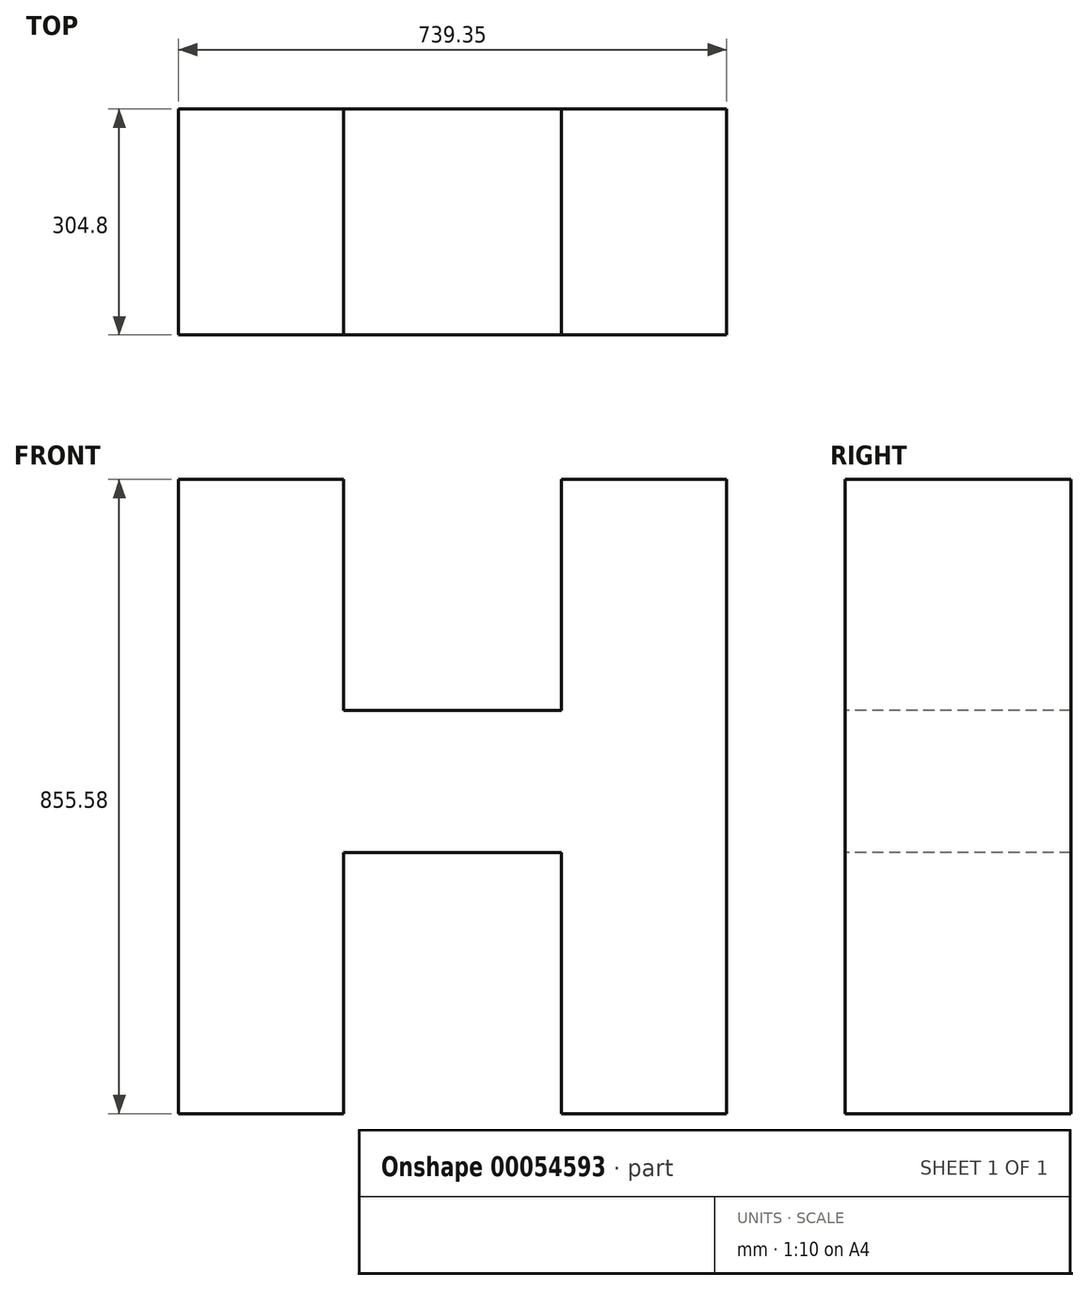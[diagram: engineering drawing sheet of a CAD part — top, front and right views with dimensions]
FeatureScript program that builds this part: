
annotation { "Feature Type Name" : "Feature", "Feature Type Description" : "" }
export const myFeature = defineFeature(function(context is Context, id is Id, definition is map)
    precondition{}
    {
        {
            var Q0;
            Q0=qCreatedBy(makeId("Front.planeOp"),FACE);
            var sketch = newSketch(context, id + "F0", { "sketchPlane" : qUnion([Q0])});
            skLineSegment(sketch, "E0", {"start": v(-331.94, 427.8) * mm, "end": v(-109.05, 427.8) * mm});
            skLineSegment(sketch, "E1", {"start": v(-109.05, 427.8) * mm, "end": v(-109.05, 116.24) * mm});
            skLineSegment(sketch, "E2", {"start": v(-109.05, 116.24) * mm, "end": v(184.53, 116.24) * mm});
            skLineSegment(sketch, "E3", {"start": v(184.53, 116.24) * mm, "end": v(184.53, 427.8) * mm});
            skLineSegment(sketch, "E4", {"start": v(184.53, 427.8) * mm, "end": v(407.4, 427.8) * mm});
            skLineSegment(sketch, "E5", {"start": v(407.4, 427.8) * mm, "end": v(407.4, -427.78) * mm});
            skLineSegment(sketch, "E6", {"start": v(407.4, -427.78) * mm, "end": v(184.53, -427.78) * mm});
            skLineSegment(sketch, "E7", {"start": v(184.53, -427.78) * mm, "end": v(184.53, -75.48) * mm});
            skLineSegment(sketch, "E8", {"start": v(184.53, -75.48) * mm, "end": v(-109.05, -75.48) * mm});
            skLineSegment(sketch, "E9", {"start": v(-109.05, -75.48) * mm, "end": v(-109.05, -427.78) * mm});
            skLineSegment(sketch, "E10", {"start": v(-109.05, -427.78) * mm, "end": v(-331.94, -427.78) * mm});
            skLineSegment(sketch, "E11", {"start": v(-331.94, -427.78) * mm, "end": v(-331.94, 427.8) * mm});
            skSolve(sketch);
        }
        {
            var Q0;
            Q0=makeQuery(id+"F0.imprint","IMPRINT",FACE,{"disambiguationData":[TD([[makeQuery(id+"F0.imprint","IMPRINT",EDGE,{"derivedFrom":sQuery(id+"F0.wireOp",EDGE,"E0")}),-1.0]])]});
            extrude(context, id + "F1", {"entities" : qUnion([Q0]), "oppositeDirection" : true, "depth" : 304.8 * mm});
        }
    });
